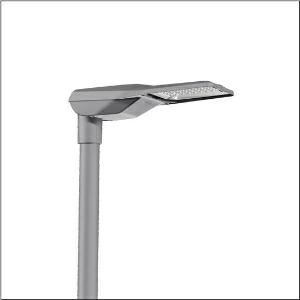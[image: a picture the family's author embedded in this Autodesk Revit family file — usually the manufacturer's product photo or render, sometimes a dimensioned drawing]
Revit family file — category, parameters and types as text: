
# Revit family: streetlight_sl_21_mini___stw1_0a_5xe6e43a08jb_3156
name_source: partatom
category: Lighting Fixtures
units: mm (PartAtom-declared; Revit-internal decimal feet)

## family parameters
Cut with Voids When Loaded = No
Host = Face
Light Source = No
Part Type = Normal
Room Calculation Point = No
Round Connector Dimension = Use Diameter
Shared = No

## types (1)
- --- (1 x LED, 13390 lm, 87.3 W, 4000K)
    Apparent Load = 87 VA
    CIE Flux Codes = 39 75 98 100 100
    Color Rendering = 70
    Color Temperature = 4000K
    Default Elevation = 1800 mm
    Description = Streetlight SL 21 mini, mast luminaire, primary light control with lens, of PMMA, primary optical cover: cover, of toughened safety glass, transparent, light distribution: STW1.0a, light emission: direct distribution, primary light characteristic: asymmetric, installation type: post-top, side-entry, LED, 3G 1.5mm², High Power LED, rated luminous flux: 13.390lm, luminous efficacy: 153lm/W, light colour: 740, colour temperature: 4000K, control: overheat protection, constant luminous flux control, time-dependent luminous flux control, flexible luminous flux parameterisation, mains connection: 230..240V, AC, 50/60Hz, connection cable pre-assembled, cable length: 10,5m, wiring characteristics: H07RN-F, start of lifetime: 87W, end of service life: 90W, reduction: 40W, luminaire housing, of diecast aluminium, powder-coated, Siteco® metallic grey (DB 702S), corrosivity category C5 mid according to DIN EN ISO 12944, please order mast flange separately, inclination adjustable: 0°, 5°, 10°, 15°, sealing non-destructively replaceable, multi-level sealing system, length: 628mm, width: 235mm, height: 110mm, mast flange for spigot size: 42mm (side-entry): 5XC10008XM4, 60/48mm (side-entry/post-top): 5XC10108XM2, 76/60mm (side-entry/post-top): 5XC10108XM1, protection rating (complete): IP66, insulation class (complete): insulation class II (safety insulation), certification: CE, ENEC, ENEC+, VDE, impact resistance: IK09, permissible operating ambient temperature for outdoor applications: -40..+50°C, standard-compliant lighting for roads and squares, packaging unit: 1 piece

Light Distribution: STW1.0a
    Height = 110 mm
    Lamp = 1 x LED
    Lamp Light Flux = 13390 lm
    Lamp Power = 87.3 W
    Lamp count = 1
    Length = 625 mm
    Luminous efficacy = 153 lm/W
    Manufacturer = Siteco
    ModVariant = No
    Model = 5XE6E43A08JB
    Number of Poles = 1
    OnlyDefault = Yes
    Power Factor = 1
    Product Name = Streetlight SL 21 mini | STW1.0a
    Product group = mast luminaire | pylon top
    ProductGroupID = 6100
    Protection Class = Protection class II
    Protection Degree = IP 66
    RLX_Detail_Level = 1
    RLX_Emergency_Light_Flux = 0 lm
    RLX_Emergency_Type = 0
    RLX_Emergency_Type_DB = No
    RlxData = <blob elided: 92333 chars, md5=bc0d65a6>
    Socket = socket
    Standby Power = 0 W
    System Light Flux = 13390 lm
    System Power = 87 W
    Type Comments = factory setting: luminous flux: 100 % | Output Level: 100 % | 915 mA
    Type Image = l_1003519.jpg
    URL = http://relux.com
    VarID = @adj_120477
    Voltage = 0 V
    Weight = 0.00 kg
    Width = 234 mm

## geometry (parser evidence)
native form markers: Blend x4, Sweep x11
no freeform markers — native parametric forms only
